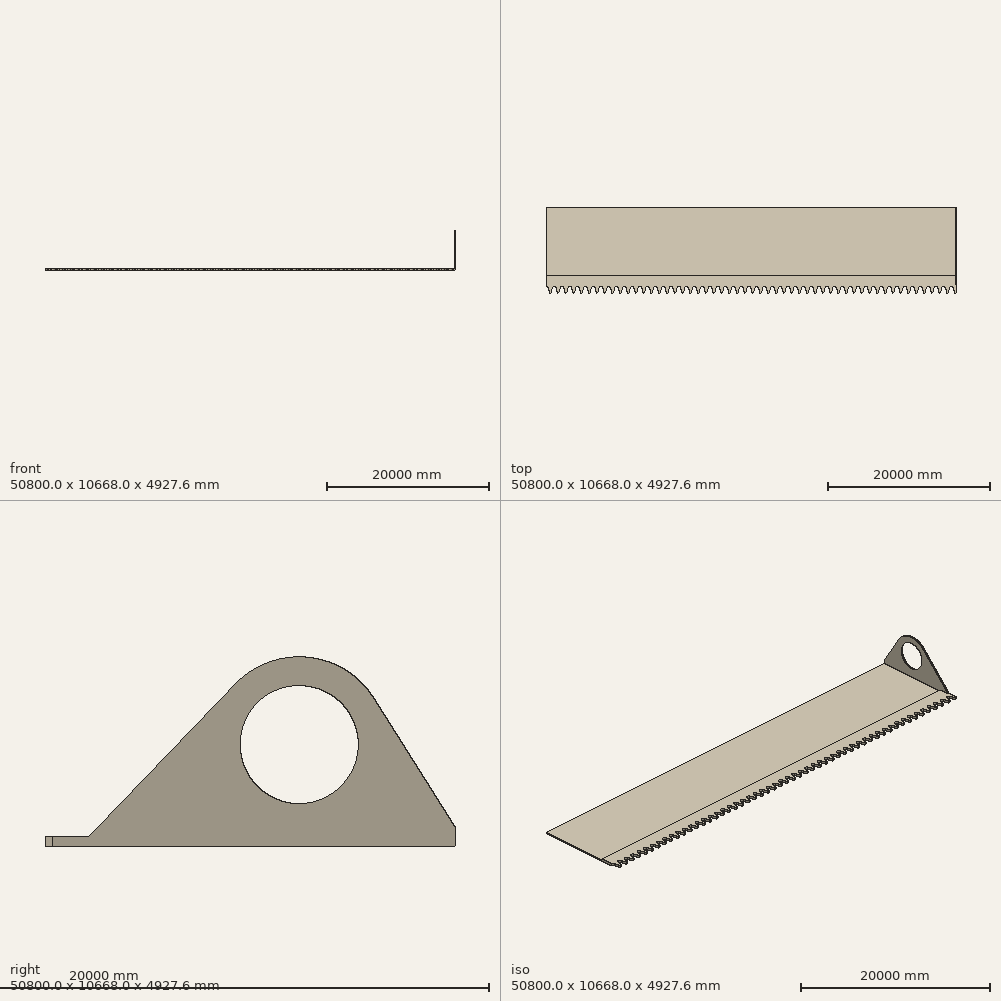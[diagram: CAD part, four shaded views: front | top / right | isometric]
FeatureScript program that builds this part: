
annotation { "Feature Type Name" : "Feature", "Feature Type Description" : "" }
export const myFeature = defineFeature(function(context is Context, id is Id, definition is map)
    precondition{}
    {
        {
            var Q0;
            Q0=qCreatedBy(makeId("Top.planeOp"),FACE);
            var sketch = newSketch(context, id + "F0", { "sketchPlane" : qUnion([Q0])});
            skLineSegment(sketch, "E0", {"start": v(-25432.17, 2645.31) * mm, "end": v(25367.83, 2645.31) * mm});
            skLineSegment(sketch, "E1", {"start": v(25367.83, 2645.31) * mm, "end": v(25367.83, -5736.69) * mm});
            skLineSegment(sketch, "E2", {"start": v(25367.83, -5736.69) * mm, "end": v(-25432.17, -5736.69) * mm});
            skLineSegment(sketch, "E3", {"start": v(-25432.17, -5736.69) * mm, "end": v(-25432.17, 2645.31) * mm});
            skSolve(sketch);
        }
        {
            var Q0;
            Q0 = qSketchRegion(id + "F0", true);
            extrude(context, id + "F1", {"entities" : qUnion([Q0]), "depth" : 101.6 * mm, "offsetDistance" : 25.4 * mm});
        }
        {
            var Q0;
            Q0=makeQuery(id+"F1.opExtrude","SWEPT_FACE",FACE,{"disambiguationData":[OSD([sQuery(id+"F0.wireOp",EDGE,"E2")])]});
            var sketch = newSketch(context, id + "F2", { "sketchPlane" : qUnion([Q0])});
            skLineSegment(sketch, "E4", {"start": v(-25432.17, 0) * mm, "end": v(-25432.17, 254) * mm});
            skLineSegment(sketch, "E5", {"start": v(-25432.17, 254) * mm, "end": v(25367.83, 254) * mm});
            skLineSegment(sketch, "E6", {"start": v(25367.83, 254) * mm, "end": v(25367.83, 0) * mm});
            skLineSegment(sketch, "E7", {"start": v(25367.83, 0) * mm, "end": v(-25432.17, 0) * mm});
            skSolve(sketch);
        }
        {
            var Q0;
            Q0 = qSketchRegion(id + "F2", true);
            extrude(context, id + "F3", {"entities" : qUnion([Q0]), "operationType" : NewBodyOperationType.ADD, "depth" : 2286 * mm, "offsetDistance" : 25.4 * mm});
        }
        {
            var Q0;
            Q0=makeQuery(id+"F3.opExtrude","SWEPT_FACE",FACE,{"disambiguationData":[OSD([sQuery(id+"F2.wireOp",EDGE,"E5")])]});
            var sketch = newSketch(context, id + "F4", { "sketchPlane" : qUnion([Q0])});
            skArc(sketch, "E8", {"start": v(-25211.32, -7328.64) * mm, "mid": v(-25292.95, -7206.36) * mm, "end": v(-25432.17, -7159.09) * mm});
            skArc(sketch, "E9", {"start": v(-24466.97, -7159.09) * mm, "mid": v(-24606.18, -7206.36) * mm, "end": v(-24687.8, -7328.64) * mm});
            skLineSegment(sketch, "E10", {"start": v(-24949.57, -8022.69) * mm, "end": v(-24873.37, -8022.69) * mm});
            skLineSegment(sketch, "E11", {"start": v(-24949.57, -8022.69) * mm, "end": v(-25025.77, -8022.69) * mm});
            skLineSegment(sketch, "E12", {"start": v(-25025.77, -8022.69) * mm, "end": v(-25211.32, -7328.64) * mm});
            skLineSegment(sketch, "E13", {"start": v(-24873.37, -8022.69) * mm, "end": v(-24687.8, -7328.64) * mm});
            skArc(sketch, "E14.1.0.0", {"start": v(-24246.12, -7328.64) * mm, "mid": v(-24327.75, -7206.36) * mm, "end": v(-24466.97, -7159.09) * mm});
            skLineSegment(sketch, "E14.1.0.1", {"start": v(-24060.57, -8022.69) * mm, "end": v(-24246.12, -7328.64) * mm});
            skLineSegment(sketch, "E14.1.0.2", {"start": v(-23984.37, -8022.69) * mm, "end": v(-24060.57, -8022.69) * mm});
            skLineSegment(sketch, "E14.1.0.3", {"start": v(-23984.37, -8022.69) * mm, "end": v(-23908.17, -8022.69) * mm});
            skLineSegment(sketch, "E14.1.0.4", {"start": v(-23908.17, -8022.69) * mm, "end": v(-23722.6, -7328.64) * mm});
            skArc(sketch, "E14.1.0.5", {"start": v(-23501.77, -7159.09) * mm, "mid": v(-23640.98, -7206.36) * mm, "end": v(-23722.6, -7328.64) * mm});
            skArc(sketch, "E14.2.0.0", {"start": v(-23280.92, -7328.64) * mm, "mid": v(-23362.55, -7206.36) * mm, "end": v(-23501.77, -7159.09) * mm});
            skLineSegment(sketch, "E14.2.0.1", {"start": v(-23095.37, -8022.69) * mm, "end": v(-23280.92, -7328.64) * mm});
            skLineSegment(sketch, "E14.2.0.2", {"start": v(-23019.17, -8022.69) * mm, "end": v(-23095.37, -8022.69) * mm});
            skLineSegment(sketch, "E14.2.0.3", {"start": v(-23019.17, -8022.69) * mm, "end": v(-22942.97, -8022.69) * mm});
            skLineSegment(sketch, "E14.2.0.4", {"start": v(-22942.97, -8022.69) * mm, "end": v(-22757.4, -7328.64) * mm});
            skArc(sketch, "E14.2.0.5", {"start": v(-22536.57, -7159.09) * mm, "mid": v(-22675.78, -7206.36) * mm, "end": v(-22757.4, -7328.64) * mm});
            skLineSegment(sketch, "E14.direction1", {"start": v(-25432.17, -7387.69) * mm, "end": v(-24466.97, -7387.69) * mm, "construction": true});
            skArc(sketch, "E15.0.3.0", {"start": v(-22315.72, -7328.64) * mm, "mid": v(-22397.35, -7206.36) * mm, "end": v(-22536.57, -7159.09) * mm});
            skLineSegment(sketch, "E15.4.3.0", {"start": v(-22130.17, -8022.69) * mm, "end": v(-22315.72, -7328.64) * mm});
            skLineSegment(sketch, "E15.7.3.0", {"start": v(-22053.97, -8022.69) * mm, "end": v(-22130.17, -8022.69) * mm});
            skLineSegment(sketch, "E15.10.3.0", {"start": v(-22053.97, -8022.69) * mm, "end": v(-21977.77, -8022.69) * mm});
            skLineSegment(sketch, "E15.13.3.0", {"start": v(-21977.77, -8022.69) * mm, "end": v(-21792.2, -7328.64) * mm});
            skArc(sketch, "E15.16.3.0", {"start": v(-21571.37, -7159.09) * mm, "mid": v(-21710.58, -7206.36) * mm, "end": v(-21792.2, -7328.64) * mm});
            skArc(sketch, "E15.0.4.0", {"start": v(-21350.52, -7328.64) * mm, "mid": v(-21432.15, -7206.36) * mm, "end": v(-21571.37, -7159.09) * mm});
            skLineSegment(sketch, "E15.4.4.0", {"start": v(-21164.97, -8022.69) * mm, "end": v(-21350.52, -7328.64) * mm});
            skLineSegment(sketch, "E15.7.4.0", {"start": v(-21088.77, -8022.69) * mm, "end": v(-21164.97, -8022.69) * mm});
            skLineSegment(sketch, "E15.10.4.0", {"start": v(-21088.77, -8022.69) * mm, "end": v(-21012.57, -8022.69) * mm});
            skLineSegment(sketch, "E15.13.4.0", {"start": v(-21012.57, -8022.69) * mm, "end": v(-20827, -7328.64) * mm});
            skArc(sketch, "E15.16.4.0", {"start": v(-20606.17, -7159.09) * mm, "mid": v(-20745.38, -7206.36) * mm, "end": v(-20827, -7328.64) * mm});
            skArc(sketch, "E15.0.5.0", {"start": v(-20385.32, -7328.64) * mm, "mid": v(-20466.95, -7206.36) * mm, "end": v(-20606.17, -7159.09) * mm});
            skLineSegment(sketch, "E15.4.5.0", {"start": v(-20199.77, -8022.69) * mm, "end": v(-20385.32, -7328.64) * mm});
            skLineSegment(sketch, "E15.7.5.0", {"start": v(-20123.57, -8022.69) * mm, "end": v(-20199.77, -8022.69) * mm});
            skLineSegment(sketch, "E15.10.5.0", {"start": v(-20123.57, -8022.69) * mm, "end": v(-20047.37, -8022.69) * mm});
            skLineSegment(sketch, "E15.13.5.0", {"start": v(-20047.37, -8022.69) * mm, "end": v(-19861.8, -7328.64) * mm});
            skArc(sketch, "E15.16.5.0", {"start": v(-19640.97, -7159.09) * mm, "mid": v(-19780.18, -7206.36) * mm, "end": v(-19861.8, -7328.64) * mm});
            skArc(sketch, "E15.0.6.0", {"start": v(-19420.12, -7328.64) * mm, "mid": v(-19501.75, -7206.36) * mm, "end": v(-19640.97, -7159.09) * mm});
            skLineSegment(sketch, "E15.4.6.0", {"start": v(-19234.57, -8022.69) * mm, "end": v(-19420.12, -7328.64) * mm});
            skLineSegment(sketch, "E15.7.6.0", {"start": v(-19158.37, -8022.69) * mm, "end": v(-19234.57, -8022.69) * mm});
            skLineSegment(sketch, "E15.10.6.0", {"start": v(-19158.37, -8022.69) * mm, "end": v(-19082.17, -8022.69) * mm});
            skLineSegment(sketch, "E15.13.6.0", {"start": v(-19082.17, -8022.69) * mm, "end": v(-18896.6, -7328.64) * mm});
            skArc(sketch, "E15.16.6.0", {"start": v(-18675.77, -7159.09) * mm, "mid": v(-18814.98, -7206.36) * mm, "end": v(-18896.6, -7328.64) * mm});
            skArc(sketch, "E15.0.7.0", {"start": v(-18454.92, -7328.64) * mm, "mid": v(-18536.55, -7206.36) * mm, "end": v(-18675.77, -7159.09) * mm});
            skLineSegment(sketch, "E15.4.7.0", {"start": v(-18269.37, -8022.69) * mm, "end": v(-18454.92, -7328.64) * mm});
            skLineSegment(sketch, "E15.7.7.0", {"start": v(-18193.17, -8022.69) * mm, "end": v(-18269.37, -8022.69) * mm});
            skLineSegment(sketch, "E15.10.7.0", {"start": v(-18193.17, -8022.69) * mm, "end": v(-18116.97, -8022.69) * mm});
            skLineSegment(sketch, "E15.13.7.0", {"start": v(-18116.97, -8022.69) * mm, "end": v(-17931.4, -7328.64) * mm});
            skArc(sketch, "E15.16.7.0", {"start": v(-17710.57, -7159.09) * mm, "mid": v(-17849.78, -7206.36) * mm, "end": v(-17931.4, -7328.64) * mm});
            skArc(sketch, "E15.0.8.0", {"start": v(-17489.72, -7328.64) * mm, "mid": v(-17571.35, -7206.36) * mm, "end": v(-17710.57, -7159.09) * mm});
            skLineSegment(sketch, "E15.4.8.0", {"start": v(-17304.17, -8022.69) * mm, "end": v(-17489.72, -7328.64) * mm});
            skLineSegment(sketch, "E15.7.8.0", {"start": v(-17227.97, -8022.69) * mm, "end": v(-17304.17, -8022.69) * mm});
            skLineSegment(sketch, "E15.10.8.0", {"start": v(-17227.97, -8022.69) * mm, "end": v(-17151.77, -8022.69) * mm});
            skLineSegment(sketch, "E15.13.8.0", {"start": v(-17151.77, -8022.69) * mm, "end": v(-16966.2, -7328.64) * mm});
            skArc(sketch, "E15.16.8.0", {"start": v(-16745.37, -7159.09) * mm, "mid": v(-16884.58, -7206.36) * mm, "end": v(-16966.2, -7328.64) * mm});
            skArc(sketch, "E15.0.9.0", {"start": v(-16524.52, -7328.64) * mm, "mid": v(-16606.15, -7206.36) * mm, "end": v(-16745.37, -7159.09) * mm});
            skLineSegment(sketch, "E15.4.9.0", {"start": v(-16338.97, -8022.69) * mm, "end": v(-16524.52, -7328.64) * mm});
            skLineSegment(sketch, "E15.7.9.0", {"start": v(-16262.77, -8022.69) * mm, "end": v(-16338.97, -8022.69) * mm});
            skLineSegment(sketch, "E15.10.9.0", {"start": v(-16262.77, -8022.69) * mm, "end": v(-16186.57, -8022.69) * mm});
            skLineSegment(sketch, "E15.13.9.0", {"start": v(-16186.57, -8022.69) * mm, "end": v(-16001, -7328.64) * mm});
            skArc(sketch, "E15.16.9.0", {"start": v(-15780.17, -7159.09) * mm, "mid": v(-15919.38, -7206.36) * mm, "end": v(-16001, -7328.64) * mm});
            skArc(sketch, "E15.0.10.0", {"start": v(-15559.32, -7328.64) * mm, "mid": v(-15640.95, -7206.36) * mm, "end": v(-15780.17, -7159.09) * mm});
            skLineSegment(sketch, "E15.4.10.0", {"start": v(-15373.77, -8022.69) * mm, "end": v(-15559.32, -7328.64) * mm});
            skLineSegment(sketch, "E15.7.10.0", {"start": v(-15297.57, -8022.69) * mm, "end": v(-15373.77, -8022.69) * mm});
            skLineSegment(sketch, "E15.10.10.0", {"start": v(-15297.57, -8022.69) * mm, "end": v(-15221.37, -8022.69) * mm});
            skLineSegment(sketch, "E15.13.10.0", {"start": v(-15221.37, -8022.69) * mm, "end": v(-15035.8, -7328.64) * mm});
            skArc(sketch, "E15.16.10.0", {"start": v(-14814.97, -7159.09) * mm, "mid": v(-14954.18, -7206.36) * mm, "end": v(-15035.8, -7328.64) * mm});
            skArc(sketch, "E15.0.11.0", {"start": v(-14594.12, -7328.64) * mm, "mid": v(-14675.75, -7206.36) * mm, "end": v(-14814.97, -7159.09) * mm});
            skLineSegment(sketch, "E15.4.11.0", {"start": v(-14408.57, -8022.69) * mm, "end": v(-14594.12, -7328.64) * mm});
            skLineSegment(sketch, "E15.7.11.0", {"start": v(-14332.37, -8022.69) * mm, "end": v(-14408.57, -8022.69) * mm});
            skLineSegment(sketch, "E15.10.11.0", {"start": v(-14332.37, -8022.69) * mm, "end": v(-14256.17, -8022.69) * mm});
            skLineSegment(sketch, "E15.13.11.0", {"start": v(-14256.17, -8022.69) * mm, "end": v(-14070.6, -7328.64) * mm});
            skArc(sketch, "E15.16.11.0", {"start": v(-13849.77, -7159.09) * mm, "mid": v(-13988.98, -7206.36) * mm, "end": v(-14070.6, -7328.64) * mm});
            skArc(sketch, "E15.0.12.0", {"start": v(-13628.92, -7328.64) * mm, "mid": v(-13710.55, -7206.36) * mm, "end": v(-13849.77, -7159.09) * mm});
            skLineSegment(sketch, "E15.4.12.0", {"start": v(-13443.37, -8022.69) * mm, "end": v(-13628.92, -7328.64) * mm});
            skLineSegment(sketch, "E15.7.12.0", {"start": v(-13367.17, -8022.69) * mm, "end": v(-13443.37, -8022.69) * mm});
            skLineSegment(sketch, "E15.10.12.0", {"start": v(-13367.17, -8022.69) * mm, "end": v(-13290.97, -8022.69) * mm});
            skLineSegment(sketch, "E15.13.12.0", {"start": v(-13290.97, -8022.69) * mm, "end": v(-13105.4, -7328.64) * mm});
            skArc(sketch, "E15.16.12.0", {"start": v(-12884.57, -7159.09) * mm, "mid": v(-13023.78, -7206.36) * mm, "end": v(-13105.4, -7328.64) * mm});
            skArc(sketch, "E15.0.13.0", {"start": v(-12663.72, -7328.64) * mm, "mid": v(-12745.35, -7206.36) * mm, "end": v(-12884.57, -7159.09) * mm});
            skLineSegment(sketch, "E15.4.13.0", {"start": v(-12478.17, -8022.69) * mm, "end": v(-12663.72, -7328.64) * mm});
            skLineSegment(sketch, "E15.7.13.0", {"start": v(-12401.97, -8022.69) * mm, "end": v(-12478.17, -8022.69) * mm});
            skLineSegment(sketch, "E15.10.13.0", {"start": v(-12401.97, -8022.69) * mm, "end": v(-12325.77, -8022.69) * mm});
            skLineSegment(sketch, "E15.13.13.0", {"start": v(-12325.77, -8022.69) * mm, "end": v(-12140.2, -7328.64) * mm});
            skArc(sketch, "E15.16.13.0", {"start": v(-11919.37, -7159.09) * mm, "mid": v(-12058.58, -7206.36) * mm, "end": v(-12140.2, -7328.64) * mm});
            skArc(sketch, "E15.0.14.0", {"start": v(-11698.52, -7328.64) * mm, "mid": v(-11780.15, -7206.36) * mm, "end": v(-11919.37, -7159.09) * mm});
            skLineSegment(sketch, "E15.4.14.0", {"start": v(-11512.97, -8022.69) * mm, "end": v(-11698.52, -7328.64) * mm});
            skLineSegment(sketch, "E15.7.14.0", {"start": v(-11436.77, -8022.69) * mm, "end": v(-11512.97, -8022.69) * mm});
            skLineSegment(sketch, "E15.10.14.0", {"start": v(-11436.77, -8022.69) * mm, "end": v(-11360.57, -8022.69) * mm});
            skLineSegment(sketch, "E15.13.14.0", {"start": v(-11360.57, -8022.69) * mm, "end": v(-11175, -7328.64) * mm});
            skArc(sketch, "E15.16.14.0", {"start": v(-10954.17, -7159.09) * mm, "mid": v(-11093.38, -7206.36) * mm, "end": v(-11175, -7328.64) * mm});
            skArc(sketch, "E15.0.15.0", {"start": v(-10733.32, -7328.64) * mm, "mid": v(-10814.95, -7206.36) * mm, "end": v(-10954.17, -7159.09) * mm});
            skLineSegment(sketch, "E15.4.15.0", {"start": v(-10547.77, -8022.69) * mm, "end": v(-10733.32, -7328.64) * mm});
            skLineSegment(sketch, "E15.7.15.0", {"start": v(-10471.57, -8022.69) * mm, "end": v(-10547.77, -8022.69) * mm});
            skLineSegment(sketch, "E15.10.15.0", {"start": v(-10471.57, -8022.69) * mm, "end": v(-10395.37, -8022.69) * mm});
            skLineSegment(sketch, "E15.13.15.0", {"start": v(-10395.37, -8022.69) * mm, "end": v(-10209.8, -7328.64) * mm});
            skArc(sketch, "E15.16.15.0", {"start": v(-9988.97, -7159.09) * mm, "mid": v(-10128.18, -7206.36) * mm, "end": v(-10209.8, -7328.64) * mm});
            skArc(sketch, "E15.0.16.0", {"start": v(-9768.12, -7328.64) * mm, "mid": v(-9849.75, -7206.36) * mm, "end": v(-9988.97, -7159.09) * mm});
            skLineSegment(sketch, "E15.4.16.0", {"start": v(-9582.57, -8022.69) * mm, "end": v(-9768.12, -7328.64) * mm});
            skLineSegment(sketch, "E15.7.16.0", {"start": v(-9506.37, -8022.69) * mm, "end": v(-9582.57, -8022.69) * mm});
            skLineSegment(sketch, "E15.10.16.0", {"start": v(-9506.37, -8022.69) * mm, "end": v(-9430.17, -8022.69) * mm});
            skLineSegment(sketch, "E15.13.16.0", {"start": v(-9430.17, -8022.69) * mm, "end": v(-9244.6, -7328.64) * mm});
            skArc(sketch, "E15.16.16.0", {"start": v(-9023.77, -7159.09) * mm, "mid": v(-9162.98, -7206.36) * mm, "end": v(-9244.6, -7328.64) * mm});
            skArc(sketch, "E15.0.17.0", {"start": v(-8802.92, -7328.64) * mm, "mid": v(-8884.55, -7206.36) * mm, "end": v(-9023.77, -7159.09) * mm});
            skLineSegment(sketch, "E15.4.17.0", {"start": v(-8617.37, -8022.69) * mm, "end": v(-8802.92, -7328.64) * mm});
            skLineSegment(sketch, "E15.7.17.0", {"start": v(-8541.17, -8022.69) * mm, "end": v(-8617.37, -8022.69) * mm});
            skLineSegment(sketch, "E15.10.17.0", {"start": v(-8541.17, -8022.69) * mm, "end": v(-8464.97, -8022.69) * mm});
            skLineSegment(sketch, "E15.13.17.0", {"start": v(-8464.97, -8022.69) * mm, "end": v(-8279.4, -7328.64) * mm});
            skArc(sketch, "E15.16.17.0", {"start": v(-8058.57, -7159.09) * mm, "mid": v(-8197.78, -7206.36) * mm, "end": v(-8279.4, -7328.64) * mm});
            skArc(sketch, "E15.0.18.0", {"start": v(-7837.72, -7328.64) * mm, "mid": v(-7919.35, -7206.36) * mm, "end": v(-8058.57, -7159.09) * mm});
            skLineSegment(sketch, "E15.4.18.0", {"start": v(-7652.17, -8022.69) * mm, "end": v(-7837.72, -7328.64) * mm});
            skLineSegment(sketch, "E15.7.18.0", {"start": v(-7575.97, -8022.69) * mm, "end": v(-7652.17, -8022.69) * mm});
            skLineSegment(sketch, "E15.10.18.0", {"start": v(-7575.97, -8022.69) * mm, "end": v(-7499.77, -8022.69) * mm});
            skLineSegment(sketch, "E15.13.18.0", {"start": v(-7499.77, -8022.69) * mm, "end": v(-7314.2, -7328.64) * mm});
            skArc(sketch, "E15.16.18.0", {"start": v(-7093.37, -7159.09) * mm, "mid": v(-7232.58, -7206.36) * mm, "end": v(-7314.2, -7328.64) * mm});
            skArc(sketch, "E15.0.19.0", {"start": v(-6872.52, -7328.64) * mm, "mid": v(-6954.15, -7206.36) * mm, "end": v(-7093.37, -7159.09) * mm});
            skLineSegment(sketch, "E15.4.19.0", {"start": v(-6686.97, -8022.69) * mm, "end": v(-6872.52, -7328.64) * mm});
            skLineSegment(sketch, "E15.7.19.0", {"start": v(-6610.77, -8022.69) * mm, "end": v(-6686.97, -8022.69) * mm});
            skLineSegment(sketch, "E15.10.19.0", {"start": v(-6610.77, -8022.69) * mm, "end": v(-6534.57, -8022.69) * mm});
            skLineSegment(sketch, "E15.13.19.0", {"start": v(-6534.57, -8022.69) * mm, "end": v(-6349, -7328.64) * mm});
            skArc(sketch, "E15.16.19.0", {"start": v(-6128.17, -7159.09) * mm, "mid": v(-6267.38, -7206.36) * mm, "end": v(-6349, -7328.64) * mm});
            skArc(sketch, "E15.0.20.0", {"start": v(-5907.32, -7328.64) * mm, "mid": v(-5988.95, -7206.36) * mm, "end": v(-6128.17, -7159.09) * mm});
            skLineSegment(sketch, "E15.4.20.0", {"start": v(-5721.77, -8022.69) * mm, "end": v(-5907.32, -7328.64) * mm});
            skLineSegment(sketch, "E15.7.20.0", {"start": v(-5645.57, -8022.69) * mm, "end": v(-5721.77, -8022.69) * mm});
            skLineSegment(sketch, "E15.10.20.0", {"start": v(-5645.57, -8022.69) * mm, "end": v(-5569.37, -8022.69) * mm});
            skLineSegment(sketch, "E15.13.20.0", {"start": v(-5569.37, -8022.69) * mm, "end": v(-5383.8, -7328.64) * mm});
            skArc(sketch, "E15.16.20.0", {"start": v(-5162.97, -7159.09) * mm, "mid": v(-5302.18, -7206.36) * mm, "end": v(-5383.8, -7328.64) * mm});
            skArc(sketch, "E15.0.21.0", {"start": v(-4942.12, -7328.64) * mm, "mid": v(-5023.75, -7206.36) * mm, "end": v(-5162.97, -7159.09) * mm});
            skLineSegment(sketch, "E15.4.21.0", {"start": v(-4756.57, -8022.69) * mm, "end": v(-4942.12, -7328.64) * mm});
            skLineSegment(sketch, "E15.7.21.0", {"start": v(-4680.37, -8022.69) * mm, "end": v(-4756.57, -8022.69) * mm});
            skLineSegment(sketch, "E15.10.21.0", {"start": v(-4680.37, -8022.69) * mm, "end": v(-4604.17, -8022.69) * mm});
            skLineSegment(sketch, "E15.13.21.0", {"start": v(-4604.17, -8022.69) * mm, "end": v(-4418.6, -7328.64) * mm});
            skArc(sketch, "E15.16.21.0", {"start": v(-4197.77, -7159.09) * mm, "mid": v(-4336.98, -7206.36) * mm, "end": v(-4418.6, -7328.64) * mm});
            skArc(sketch, "E15.0.22.0", {"start": v(-3976.92, -7328.64) * mm, "mid": v(-4058.55, -7206.36) * mm, "end": v(-4197.77, -7159.09) * mm});
            skLineSegment(sketch, "E15.4.22.0", {"start": v(-3791.37, -8022.69) * mm, "end": v(-3976.92, -7328.64) * mm});
            skLineSegment(sketch, "E15.7.22.0", {"start": v(-3715.17, -8022.69) * mm, "end": v(-3791.37, -8022.69) * mm});
            skLineSegment(sketch, "E15.10.22.0", {"start": v(-3715.17, -8022.69) * mm, "end": v(-3638.97, -8022.69) * mm});
            skLineSegment(sketch, "E15.13.22.0", {"start": v(-3638.97, -8022.69) * mm, "end": v(-3453.4, -7328.64) * mm});
            skArc(sketch, "E15.16.22.0", {"start": v(-3232.57, -7159.09) * mm, "mid": v(-3371.78, -7206.36) * mm, "end": v(-3453.4, -7328.64) * mm});
            skArc(sketch, "E15.0.23.0", {"start": v(-3011.72, -7328.64) * mm, "mid": v(-3093.35, -7206.36) * mm, "end": v(-3232.57, -7159.09) * mm});
            skLineSegment(sketch, "E15.4.23.0", {"start": v(-2826.17, -8022.69) * mm, "end": v(-3011.72, -7328.64) * mm});
            skLineSegment(sketch, "E15.7.23.0", {"start": v(-2749.97, -8022.69) * mm, "end": v(-2826.17, -8022.69) * mm});
            skLineSegment(sketch, "E15.10.23.0", {"start": v(-2749.97, -8022.69) * mm, "end": v(-2673.77, -8022.69) * mm});
            skLineSegment(sketch, "E15.13.23.0", {"start": v(-2673.77, -8022.69) * mm, "end": v(-2488.2, -7328.64) * mm});
            skArc(sketch, "E15.16.23.0", {"start": v(-2267.37, -7159.09) * mm, "mid": v(-2406.58, -7206.36) * mm, "end": v(-2488.2, -7328.64) * mm});
            skArc(sketch, "E15.0.24.0", {"start": v(-2046.52, -7328.64) * mm, "mid": v(-2128.15, -7206.36) * mm, "end": v(-2267.37, -7159.09) * mm});
            skLineSegment(sketch, "E15.4.24.0", {"start": v(-1860.97, -8022.69) * mm, "end": v(-2046.52, -7328.64) * mm});
            skLineSegment(sketch, "E15.7.24.0", {"start": v(-1784.77, -8022.69) * mm, "end": v(-1860.97, -8022.69) * mm});
            skLineSegment(sketch, "E15.10.24.0", {"start": v(-1784.77, -8022.69) * mm, "end": v(-1708.57, -8022.69) * mm});
            skLineSegment(sketch, "E15.13.24.0", {"start": v(-1708.57, -8022.69) * mm, "end": v(-1523, -7328.64) * mm});
            skArc(sketch, "E15.16.24.0", {"start": v(-1302.17, -7159.09) * mm, "mid": v(-1441.38, -7206.36) * mm, "end": v(-1523, -7328.64) * mm});
            skArc(sketch, "E15.0.25.0", {"start": v(-1081.32, -7328.64) * mm, "mid": v(-1162.95, -7206.36) * mm, "end": v(-1302.17, -7159.09) * mm});
            skLineSegment(sketch, "E15.4.25.0", {"start": v(-895.77, -8022.69) * mm, "end": v(-1081.32, -7328.64) * mm});
            skLineSegment(sketch, "E15.7.25.0", {"start": v(-819.57, -8022.69) * mm, "end": v(-895.77, -8022.69) * mm});
            skLineSegment(sketch, "E15.10.25.0", {"start": v(-819.57, -8022.69) * mm, "end": v(-743.37, -8022.69) * mm});
            skLineSegment(sketch, "E15.13.25.0", {"start": v(-743.37, -8022.69) * mm, "end": v(-557.8, -7328.64) * mm});
            skArc(sketch, "E15.16.25.0", {"start": v(-336.97, -7159.09) * mm, "mid": v(-476.18, -7206.36) * mm, "end": v(-557.8, -7328.64) * mm});
            skArc(sketch, "E15.0.26.0", {"start": v(-116.12, -7328.64) * mm, "mid": v(-197.75, -7206.36) * mm, "end": v(-336.97, -7159.09) * mm});
            skLineSegment(sketch, "E15.4.26.0", {"start": v(69.43, -8022.69) * mm, "end": v(-116.12, -7328.64) * mm});
            skLineSegment(sketch, "E15.7.26.0", {"start": v(145.63, -8022.69) * mm, "end": v(69.43, -8022.69) * mm});
            skLineSegment(sketch, "E15.10.26.0", {"start": v(145.63, -8022.69) * mm, "end": v(221.83, -8022.69) * mm});
            skLineSegment(sketch, "E15.13.26.0", {"start": v(221.83, -8022.69) * mm, "end": v(407.4, -7328.64) * mm});
            skArc(sketch, "E15.16.26.0", {"start": v(628.23, -7159.09) * mm, "mid": v(489.02, -7206.36) * mm, "end": v(407.4, -7328.64) * mm});
            skArc(sketch, "E15.0.27.0", {"start": v(849.08, -7328.64) * mm, "mid": v(767.45, -7206.36) * mm, "end": v(628.23, -7159.09) * mm});
            skLineSegment(sketch, "E15.4.27.0", {"start": v(1034.63, -8022.69) * mm, "end": v(849.08, -7328.64) * mm});
            skLineSegment(sketch, "E15.7.27.0", {"start": v(1110.83, -8022.69) * mm, "end": v(1034.63, -8022.69) * mm});
            skLineSegment(sketch, "E15.10.27.0", {"start": v(1110.83, -8022.69) * mm, "end": v(1187.03, -8022.69) * mm});
            skLineSegment(sketch, "E15.13.27.0", {"start": v(1187.03, -8022.69) * mm, "end": v(1372.6, -7328.64) * mm});
            skArc(sketch, "E15.16.27.0", {"start": v(1593.43, -7159.09) * mm, "mid": v(1454.22, -7206.36) * mm, "end": v(1372.6, -7328.64) * mm});
            skArc(sketch, "E15.0.28.0", {"start": v(1814.28, -7328.64) * mm, "mid": v(1732.65, -7206.36) * mm, "end": v(1593.43, -7159.09) * mm});
            skLineSegment(sketch, "E15.4.28.0", {"start": v(1999.83, -8022.69) * mm, "end": v(1814.28, -7328.64) * mm});
            skLineSegment(sketch, "E15.7.28.0", {"start": v(2076.03, -8022.69) * mm, "end": v(1999.83, -8022.69) * mm});
            skLineSegment(sketch, "E15.10.28.0", {"start": v(2076.03, -8022.69) * mm, "end": v(2152.23, -8022.69) * mm});
            skLineSegment(sketch, "E15.13.28.0", {"start": v(2152.23, -8022.69) * mm, "end": v(2337.8, -7328.64) * mm});
            skArc(sketch, "E15.16.28.0", {"start": v(2558.63, -7159.09) * mm, "mid": v(2419.42, -7206.36) * mm, "end": v(2337.8, -7328.64) * mm});
            skArc(sketch, "E15.0.29.0", {"start": v(2779.48, -7328.64) * mm, "mid": v(2697.85, -7206.36) * mm, "end": v(2558.63, -7159.09) * mm});
            skLineSegment(sketch, "E15.4.29.0", {"start": v(2965.03, -8022.69) * mm, "end": v(2779.48, -7328.64) * mm});
            skLineSegment(sketch, "E15.7.29.0", {"start": v(3041.23, -8022.69) * mm, "end": v(2965.03, -8022.69) * mm});
            skLineSegment(sketch, "E15.10.29.0", {"start": v(3041.23, -8022.69) * mm, "end": v(3117.43, -8022.69) * mm});
            skLineSegment(sketch, "E15.13.29.0", {"start": v(3117.43, -8022.69) * mm, "end": v(3303, -7328.64) * mm});
            skArc(sketch, "E15.16.29.0", {"start": v(3523.83, -7159.09) * mm, "mid": v(3384.62, -7206.36) * mm, "end": v(3303, -7328.64) * mm});
            skArc(sketch, "E15.0.30.0", {"start": v(3744.68, -7328.64) * mm, "mid": v(3663.05, -7206.36) * mm, "end": v(3523.83, -7159.09) * mm});
            skLineSegment(sketch, "E15.4.30.0", {"start": v(3930.23, -8022.69) * mm, "end": v(3744.68, -7328.64) * mm});
            skLineSegment(sketch, "E15.7.30.0", {"start": v(4006.43, -8022.69) * mm, "end": v(3930.23, -8022.69) * mm});
            skLineSegment(sketch, "E15.10.30.0", {"start": v(4006.43, -8022.69) * mm, "end": v(4082.63, -8022.69) * mm});
            skLineSegment(sketch, "E15.13.30.0", {"start": v(4082.63, -8022.69) * mm, "end": v(4268.2, -7328.64) * mm});
            skArc(sketch, "E15.16.30.0", {"start": v(4489.03, -7159.09) * mm, "mid": v(4349.82, -7206.36) * mm, "end": v(4268.2, -7328.64) * mm});
            skArc(sketch, "E15.0.31.0", {"start": v(4709.88, -7328.64) * mm, "mid": v(4628.25, -7206.36) * mm, "end": v(4489.03, -7159.09) * mm});
            skLineSegment(sketch, "E15.4.31.0", {"start": v(4895.43, -8022.69) * mm, "end": v(4709.88, -7328.64) * mm});
            skLineSegment(sketch, "E15.7.31.0", {"start": v(4971.63, -8022.69) * mm, "end": v(4895.43, -8022.69) * mm});
            skLineSegment(sketch, "E15.10.31.0", {"start": v(4971.63, -8022.69) * mm, "end": v(5047.83, -8022.69) * mm});
            skLineSegment(sketch, "E15.13.31.0", {"start": v(5047.83, -8022.69) * mm, "end": v(5233.4, -7328.64) * mm});
            skArc(sketch, "E15.16.31.0", {"start": v(5454.23, -7159.09) * mm, "mid": v(5315.02, -7206.36) * mm, "end": v(5233.4, -7328.64) * mm});
            skArc(sketch, "E15.0.32.0", {"start": v(5675.08, -7328.64) * mm, "mid": v(5593.45, -7206.36) * mm, "end": v(5454.23, -7159.09) * mm});
            skLineSegment(sketch, "E15.4.32.0", {"start": v(5860.63, -8022.69) * mm, "end": v(5675.08, -7328.64) * mm});
            skLineSegment(sketch, "E15.7.32.0", {"start": v(5936.83, -8022.69) * mm, "end": v(5860.63, -8022.69) * mm});
            skLineSegment(sketch, "E15.10.32.0", {"start": v(5936.83, -8022.69) * mm, "end": v(6013.03, -8022.69) * mm});
            skLineSegment(sketch, "E15.13.32.0", {"start": v(6013.03, -8022.69) * mm, "end": v(6198.6, -7328.64) * mm});
            skArc(sketch, "E15.16.32.0", {"start": v(6419.43, -7159.09) * mm, "mid": v(6280.22, -7206.36) * mm, "end": v(6198.6, -7328.64) * mm});
            skArc(sketch, "E15.0.33.0", {"start": v(6640.28, -7328.64) * mm, "mid": v(6558.65, -7206.36) * mm, "end": v(6419.43, -7159.09) * mm});
            skLineSegment(sketch, "E15.4.33.0", {"start": v(6825.83, -8022.69) * mm, "end": v(6640.28, -7328.64) * mm});
            skLineSegment(sketch, "E15.7.33.0", {"start": v(6902.03, -8022.69) * mm, "end": v(6825.83, -8022.69) * mm});
            skLineSegment(sketch, "E15.10.33.0", {"start": v(6902.03, -8022.69) * mm, "end": v(6978.23, -8022.69) * mm});
            skLineSegment(sketch, "E15.13.33.0", {"start": v(6978.23, -8022.69) * mm, "end": v(7163.8, -7328.64) * mm});
            skArc(sketch, "E15.16.33.0", {"start": v(7384.63, -7159.09) * mm, "mid": v(7245.42, -7206.36) * mm, "end": v(7163.8, -7328.64) * mm});
            skArc(sketch, "E15.0.34.0", {"start": v(7605.48, -7328.64) * mm, "mid": v(7523.85, -7206.36) * mm, "end": v(7384.63, -7159.09) * mm});
            skLineSegment(sketch, "E15.4.34.0", {"start": v(7791.03, -8022.69) * mm, "end": v(7605.48, -7328.64) * mm});
            skLineSegment(sketch, "E15.7.34.0", {"start": v(7867.23, -8022.69) * mm, "end": v(7791.03, -8022.69) * mm});
            skLineSegment(sketch, "E15.10.34.0", {"start": v(7867.23, -8022.69) * mm, "end": v(7943.43, -8022.69) * mm});
            skLineSegment(sketch, "E15.13.34.0", {"start": v(7943.43, -8022.69) * mm, "end": v(8129, -7328.64) * mm});
            skArc(sketch, "E15.16.34.0", {"start": v(8349.83, -7159.09) * mm, "mid": v(8210.62, -7206.36) * mm, "end": v(8129, -7328.64) * mm});
            skArc(sketch, "E15.0.35.0", {"start": v(8570.68, -7328.64) * mm, "mid": v(8489.05, -7206.36) * mm, "end": v(8349.83, -7159.09) * mm});
            skLineSegment(sketch, "E15.4.35.0", {"start": v(8756.23, -8022.69) * mm, "end": v(8570.68, -7328.64) * mm});
            skLineSegment(sketch, "E15.7.35.0", {"start": v(8832.43, -8022.69) * mm, "end": v(8756.23, -8022.69) * mm});
            skLineSegment(sketch, "E15.10.35.0", {"start": v(8832.43, -8022.69) * mm, "end": v(8908.63, -8022.69) * mm});
            skLineSegment(sketch, "E15.13.35.0", {"start": v(8908.63, -8022.69) * mm, "end": v(9094.2, -7328.64) * mm});
            skArc(sketch, "E15.16.35.0", {"start": v(9315.03, -7159.09) * mm, "mid": v(9175.82, -7206.36) * mm, "end": v(9094.2, -7328.64) * mm});
            skArc(sketch, "E15.0.36.0", {"start": v(9535.88, -7328.64) * mm, "mid": v(9454.25, -7206.36) * mm, "end": v(9315.03, -7159.09) * mm});
            skLineSegment(sketch, "E15.4.36.0", {"start": v(9721.43, -8022.69) * mm, "end": v(9535.88, -7328.64) * mm});
            skLineSegment(sketch, "E15.7.36.0", {"start": v(9797.63, -8022.69) * mm, "end": v(9721.43, -8022.69) * mm});
            skLineSegment(sketch, "E15.10.36.0", {"start": v(9797.63, -8022.69) * mm, "end": v(9873.83, -8022.69) * mm});
            skLineSegment(sketch, "E15.13.36.0", {"start": v(9873.83, -8022.69) * mm, "end": v(10059.4, -7328.64) * mm});
            skArc(sketch, "E15.16.36.0", {"start": v(10280.23, -7159.09) * mm, "mid": v(10141.02, -7206.36) * mm, "end": v(10059.4, -7328.64) * mm});
            skArc(sketch, "E15.0.37.0", {"start": v(10501.08, -7328.64) * mm, "mid": v(10419.45, -7206.36) * mm, "end": v(10280.23, -7159.09) * mm});
            skLineSegment(sketch, "E15.4.37.0", {"start": v(10686.63, -8022.69) * mm, "end": v(10501.08, -7328.64) * mm});
            skLineSegment(sketch, "E15.7.37.0", {"start": v(10762.83, -8022.69) * mm, "end": v(10686.63, -8022.69) * mm});
            skLineSegment(sketch, "E15.10.37.0", {"start": v(10762.83, -8022.69) * mm, "end": v(10839.03, -8022.69) * mm});
            skLineSegment(sketch, "E15.13.37.0", {"start": v(10839.03, -8022.69) * mm, "end": v(11024.6, -7328.64) * mm});
            skArc(sketch, "E15.16.37.0", {"start": v(11245.43, -7159.09) * mm, "mid": v(11106.22, -7206.36) * mm, "end": v(11024.6, -7328.64) * mm});
            skArc(sketch, "E15.0.38.0", {"start": v(11466.28, -7328.64) * mm, "mid": v(11384.65, -7206.36) * mm, "end": v(11245.43, -7159.09) * mm});
            skLineSegment(sketch, "E15.4.38.0", {"start": v(11651.83, -8022.69) * mm, "end": v(11466.28, -7328.64) * mm});
            skLineSegment(sketch, "E15.7.38.0", {"start": v(11728.03, -8022.69) * mm, "end": v(11651.83, -8022.69) * mm});
            skLineSegment(sketch, "E15.10.38.0", {"start": v(11728.03, -8022.69) * mm, "end": v(11804.23, -8022.69) * mm});
            skLineSegment(sketch, "E15.13.38.0", {"start": v(11804.23, -8022.69) * mm, "end": v(11989.8, -7328.64) * mm});
            skArc(sketch, "E15.16.38.0", {"start": v(12210.63, -7159.09) * mm, "mid": v(12071.42, -7206.36) * mm, "end": v(11989.8, -7328.64) * mm});
            skArc(sketch, "E15.0.39.0", {"start": v(12431.48, -7328.64) * mm, "mid": v(12349.85, -7206.36) * mm, "end": v(12210.63, -7159.09) * mm});
            skLineSegment(sketch, "E15.4.39.0", {"start": v(12617.03, -8022.69) * mm, "end": v(12431.48, -7328.64) * mm});
            skLineSegment(sketch, "E15.7.39.0", {"start": v(12693.23, -8022.69) * mm, "end": v(12617.03, -8022.69) * mm});
            skLineSegment(sketch, "E15.10.39.0", {"start": v(12693.23, -8022.69) * mm, "end": v(12769.43, -8022.69) * mm});
            skLineSegment(sketch, "E15.13.39.0", {"start": v(12769.43, -8022.69) * mm, "end": v(12955, -7328.64) * mm});
            skArc(sketch, "E15.16.39.0", {"start": v(13175.83, -7159.09) * mm, "mid": v(13036.62, -7206.36) * mm, "end": v(12955, -7328.64) * mm});
            skArc(sketch, "E15.0.40.0", {"start": v(13396.68, -7328.64) * mm, "mid": v(13315.05, -7206.36) * mm, "end": v(13175.83, -7159.09) * mm});
            skLineSegment(sketch, "E15.4.40.0", {"start": v(13582.23, -8022.69) * mm, "end": v(13396.68, -7328.64) * mm});
            skLineSegment(sketch, "E15.7.40.0", {"start": v(13658.43, -8022.69) * mm, "end": v(13582.23, -8022.69) * mm});
            skLineSegment(sketch, "E15.10.40.0", {"start": v(13658.43, -8022.69) * mm, "end": v(13734.63, -8022.69) * mm});
            skLineSegment(sketch, "E15.13.40.0", {"start": v(13734.63, -8022.69) * mm, "end": v(13920.2, -7328.64) * mm});
            skArc(sketch, "E15.16.40.0", {"start": v(14141.03, -7159.09) * mm, "mid": v(14001.82, -7206.36) * mm, "end": v(13920.2, -7328.64) * mm});
            skArc(sketch, "E15.0.41.0", {"start": v(14361.88, -7328.64) * mm, "mid": v(14280.25, -7206.36) * mm, "end": v(14141.03, -7159.09) * mm});
            skLineSegment(sketch, "E15.4.41.0", {"start": v(14547.43, -8022.69) * mm, "end": v(14361.88, -7328.64) * mm});
            skLineSegment(sketch, "E15.7.41.0", {"start": v(14623.63, -8022.69) * mm, "end": v(14547.43, -8022.69) * mm});
            skLineSegment(sketch, "E15.10.41.0", {"start": v(14623.63, -8022.69) * mm, "end": v(14699.83, -8022.69) * mm});
            skLineSegment(sketch, "E15.13.41.0", {"start": v(14699.83, -8022.69) * mm, "end": v(14885.4, -7328.64) * mm});
            skArc(sketch, "E15.16.41.0", {"start": v(15106.23, -7159.09) * mm, "mid": v(14967.02, -7206.36) * mm, "end": v(14885.4, -7328.64) * mm});
            skArc(sketch, "E15.0.42.0", {"start": v(15327.08, -7328.64) * mm, "mid": v(15245.45, -7206.36) * mm, "end": v(15106.23, -7159.09) * mm});
            skLineSegment(sketch, "E15.4.42.0", {"start": v(15512.63, -8022.69) * mm, "end": v(15327.08, -7328.64) * mm});
            skLineSegment(sketch, "E15.7.42.0", {"start": v(15588.83, -8022.69) * mm, "end": v(15512.63, -8022.69) * mm});
            skLineSegment(sketch, "E15.10.42.0", {"start": v(15588.83, -8022.69) * mm, "end": v(15665.03, -8022.69) * mm});
            skLineSegment(sketch, "E15.13.42.0", {"start": v(15665.03, -8022.69) * mm, "end": v(15850.6, -7328.64) * mm});
            skArc(sketch, "E15.16.42.0", {"start": v(16071.43, -7159.09) * mm, "mid": v(15932.22, -7206.36) * mm, "end": v(15850.6, -7328.64) * mm});
            skArc(sketch, "E15.0.43.0", {"start": v(16292.28, -7328.64) * mm, "mid": v(16210.65, -7206.36) * mm, "end": v(16071.43, -7159.09) * mm});
            skLineSegment(sketch, "E15.4.43.0", {"start": v(16477.83, -8022.69) * mm, "end": v(16292.28, -7328.64) * mm});
            skLineSegment(sketch, "E15.7.43.0", {"start": v(16554.03, -8022.69) * mm, "end": v(16477.83, -8022.69) * mm});
            skLineSegment(sketch, "E15.10.43.0", {"start": v(16554.03, -8022.69) * mm, "end": v(16630.23, -8022.69) * mm});
            skLineSegment(sketch, "E15.13.43.0", {"start": v(16630.23, -8022.69) * mm, "end": v(16815.8, -7328.64) * mm});
            skArc(sketch, "E15.16.43.0", {"start": v(17036.63, -7159.09) * mm, "mid": v(16897.42, -7206.36) * mm, "end": v(16815.8, -7328.64) * mm});
            skArc(sketch, "E15.0.44.0", {"start": v(17257.48, -7328.64) * mm, "mid": v(17175.85, -7206.36) * mm, "end": v(17036.63, -7159.09) * mm});
            skLineSegment(sketch, "E15.4.44.0", {"start": v(17443.03, -8022.69) * mm, "end": v(17257.48, -7328.64) * mm});
            skLineSegment(sketch, "E15.7.44.0", {"start": v(17519.23, -8022.69) * mm, "end": v(17443.03, -8022.69) * mm});
            skLineSegment(sketch, "E15.10.44.0", {"start": v(17519.23, -8022.69) * mm, "end": v(17595.43, -8022.69) * mm});
            skLineSegment(sketch, "E15.13.44.0", {"start": v(17595.43, -8022.69) * mm, "end": v(17781, -7328.64) * mm});
            skArc(sketch, "E15.16.44.0", {"start": v(18001.83, -7159.09) * mm, "mid": v(17862.62, -7206.36) * mm, "end": v(17781, -7328.64) * mm});
            skArc(sketch, "E15.0.45.0", {"start": v(18222.68, -7328.64) * mm, "mid": v(18141.05, -7206.36) * mm, "end": v(18001.83, -7159.09) * mm});
            skLineSegment(sketch, "E15.4.45.0", {"start": v(18408.23, -8022.69) * mm, "end": v(18222.68, -7328.64) * mm});
            skLineSegment(sketch, "E15.7.45.0", {"start": v(18484.43, -8022.69) * mm, "end": v(18408.23, -8022.69) * mm});
            skLineSegment(sketch, "E15.10.45.0", {"start": v(18484.43, -8022.69) * mm, "end": v(18560.63, -8022.69) * mm});
            skLineSegment(sketch, "E15.13.45.0", {"start": v(18560.63, -8022.69) * mm, "end": v(18746.2, -7328.64) * mm});
            skArc(sketch, "E15.16.45.0", {"start": v(18967.03, -7159.09) * mm, "mid": v(18827.82, -7206.36) * mm, "end": v(18746.2, -7328.64) * mm});
            skArc(sketch, "E15.0.46.0", {"start": v(19187.88, -7328.64) * mm, "mid": v(19106.25, -7206.36) * mm, "end": v(18967.03, -7159.09) * mm});
            skLineSegment(sketch, "E15.4.46.0", {"start": v(19373.43, -8022.69) * mm, "end": v(19187.88, -7328.64) * mm});
            skLineSegment(sketch, "E15.7.46.0", {"start": v(19449.63, -8022.69) * mm, "end": v(19373.43, -8022.69) * mm});
            skLineSegment(sketch, "E15.10.46.0", {"start": v(19449.63, -8022.69) * mm, "end": v(19525.83, -8022.69) * mm});
            skLineSegment(sketch, "E15.13.46.0", {"start": v(19525.83, -8022.69) * mm, "end": v(19711.4, -7328.64) * mm});
            skArc(sketch, "E15.16.46.0", {"start": v(19932.23, -7159.09) * mm, "mid": v(19793.02, -7206.36) * mm, "end": v(19711.4, -7328.64) * mm});
            skArc(sketch, "E15.0.47.0", {"start": v(20153.08, -7328.64) * mm, "mid": v(20071.45, -7206.36) * mm, "end": v(19932.23, -7159.09) * mm});
            skLineSegment(sketch, "E15.4.47.0", {"start": v(20338.63, -8022.69) * mm, "end": v(20153.08, -7328.64) * mm});
            skLineSegment(sketch, "E15.7.47.0", {"start": v(20414.83, -8022.69) * mm, "end": v(20338.63, -8022.69) * mm});
            skLineSegment(sketch, "E15.10.47.0", {"start": v(20414.83, -8022.69) * mm, "end": v(20491.03, -8022.69) * mm});
            skLineSegment(sketch, "E15.13.47.0", {"start": v(20491.03, -8022.69) * mm, "end": v(20676.6, -7328.64) * mm});
            skArc(sketch, "E15.16.47.0", {"start": v(20897.43, -7159.09) * mm, "mid": v(20758.22, -7206.36) * mm, "end": v(20676.6, -7328.64) * mm});
            skArc(sketch, "E15.0.48.0", {"start": v(21118.28, -7328.64) * mm, "mid": v(21036.65, -7206.36) * mm, "end": v(20897.43, -7159.09) * mm});
            skLineSegment(sketch, "E15.4.48.0", {"start": v(21303.83, -8022.69) * mm, "end": v(21118.28, -7328.64) * mm});
            skLineSegment(sketch, "E15.7.48.0", {"start": v(21380.03, -8022.69) * mm, "end": v(21303.83, -8022.69) * mm});
            skLineSegment(sketch, "E15.10.48.0", {"start": v(21380.03, -8022.69) * mm, "end": v(21456.23, -8022.69) * mm});
            skLineSegment(sketch, "E15.13.48.0", {"start": v(21456.23, -8022.69) * mm, "end": v(21641.8, -7328.64) * mm});
            skArc(sketch, "E15.16.48.0", {"start": v(21862.63, -7159.09) * mm, "mid": v(21723.42, -7206.36) * mm, "end": v(21641.8, -7328.64) * mm});
            skArc(sketch, "E15.0.49.0", {"start": v(22083.48, -7328.64) * mm, "mid": v(22001.85, -7206.36) * mm, "end": v(21862.63, -7159.09) * mm});
            skLineSegment(sketch, "E15.4.49.0", {"start": v(22269.03, -8022.69) * mm, "end": v(22083.48, -7328.64) * mm});
            skLineSegment(sketch, "E15.7.49.0", {"start": v(22345.23, -8022.69) * mm, "end": v(22269.03, -8022.69) * mm});
            skLineSegment(sketch, "E15.10.49.0", {"start": v(22345.23, -8022.69) * mm, "end": v(22421.43, -8022.69) * mm});
            skLineSegment(sketch, "E15.13.49.0", {"start": v(22421.43, -8022.69) * mm, "end": v(22607, -7328.64) * mm});
            skArc(sketch, "E15.16.49.0", {"start": v(22827.83, -7159.09) * mm, "mid": v(22688.62, -7206.36) * mm, "end": v(22607, -7328.64) * mm});
            skArc(sketch, "E15.0.50.0", {"start": v(23048.68, -7328.64) * mm, "mid": v(22967.05, -7206.36) * mm, "end": v(22827.83, -7159.09) * mm});
            skLineSegment(sketch, "E15.4.50.0", {"start": v(23234.23, -8022.69) * mm, "end": v(23048.68, -7328.64) * mm});
            skLineSegment(sketch, "E15.7.50.0", {"start": v(23310.43, -8022.69) * mm, "end": v(23234.23, -8022.69) * mm});
            skLineSegment(sketch, "E15.10.50.0", {"start": v(23310.43, -8022.69) * mm, "end": v(23386.63, -8022.69) * mm});
            skLineSegment(sketch, "E15.13.50.0", {"start": v(23386.63, -8022.69) * mm, "end": v(23572.2, -7328.64) * mm});
            skArc(sketch, "E15.16.50.0", {"start": v(23793.03, -7159.09) * mm, "mid": v(23653.82, -7206.36) * mm, "end": v(23572.2, -7328.64) * mm});
            skArc(sketch, "E15.0.51.0", {"start": v(24013.88, -7328.64) * mm, "mid": v(23932.25, -7206.36) * mm, "end": v(23793.03, -7159.09) * mm});
            skLineSegment(sketch, "E15.4.51.0", {"start": v(24199.43, -8022.69) * mm, "end": v(24013.88, -7328.64) * mm});
            skLineSegment(sketch, "E15.7.51.0", {"start": v(24275.63, -8022.69) * mm, "end": v(24199.43, -8022.69) * mm});
            skLineSegment(sketch, "E15.10.51.0", {"start": v(24275.63, -8022.69) * mm, "end": v(24351.83, -8022.69) * mm});
            skLineSegment(sketch, "E15.13.51.0", {"start": v(24351.83, -8022.69) * mm, "end": v(24537.4, -7328.64) * mm});
            skArc(sketch, "E15.16.51.0", {"start": v(24758.23, -7159.09) * mm, "mid": v(24619.02, -7206.36) * mm, "end": v(24537.4, -7328.64) * mm});
            skArc(sketch, "E15.0.52.0", {"start": v(24979.08, -7328.64) * mm, "mid": v(24897.45, -7206.36) * mm, "end": v(24758.23, -7159.09) * mm});
            skLineSegment(sketch, "E15.4.52.0", {"start": v(25164.63, -8022.69) * mm, "end": v(24979.08, -7328.64) * mm});
            skLineSegment(sketch, "E15.7.52.0", {"start": v(25240.83, -8022.69) * mm, "end": v(25164.63, -8022.69) * mm});
            skLineSegment(sketch, "E15.10.52.0", {"start": v(25240.83, -8022.69) * mm, "end": v(25317.03, -8022.69) * mm});
            skLineSegment(sketch, "E15.13.52.0", {"start": v(25317.03, -8022.69) * mm, "end": v(25502.6, -7328.64) * mm});
            skArc(sketch, "E15.16.52.0", {"start": v(25723.43, -7159.09) * mm, "mid": v(25584.22, -7206.36) * mm, "end": v(25502.6, -7328.64) * mm});
            skLineSegment(sketch, "E16", {"start": v(25367.83, -7832.68) * mm, "end": v(25367.83, -8162.97) * mm});
            skLineSegment(sketch, "E17", {"start": v(25367.83, -8162.97) * mm, "end": v(-25432.17, -8162.97) * mm});
            skLineSegment(sketch, "E18", {"start": v(-25432.17, -8162.97) * mm, "end": v(-25432.17, -7159.09) * mm});
            skSolve(sketch);
        }
        {
            var Q0;
            Q0 = qSketchRegion(id + "F4", true);
            extrude(context, id + "F5", {"entities" : qUnion([Q0]), "operationType" : NewBodyOperationType.REMOVE, "oppositeDirection" : true, "depth" : 254 * mm, "offsetDistance" : 25.4 * mm});
        }
        {
            var Q0;
            Q0=makeQuery(id+"F3.boolean.opBoolean","MERGE",FACE,{"derivedFrom":[makeQuery(id+"F1.opExtrude","SWEPT_FACE",FACE,{"disambiguationData":[OSD([sQuery(id+"F0.wireOp",EDGE,"E1")])]}),makeQuery(id+"F3.opExtrude","SWEPT_FACE",FACE,{"disambiguationData":[OSD([sQuery(id+"F2.wireOp",EDGE,"E6")])]})]});
            var sketch = newSketch(context, id + "F6", { "sketchPlane" : qUnion([Q0])});
            skLineSegment(sketch, "E19", {"start": v(-5736.69, 254) * mm, "end": v(-6879.69, 254) * mm});
            skLineSegment(sketch, "E20", {"start": v(-5736.69, 254) * mm, "end": v(-5736.69, 101.6) * mm});
            skLineSegment(sketch, "E21", {"start": v(-5736.69, 101.6) * mm, "end": v(2645.31, 101.6) * mm});
            skLineSegment(sketch, "E22", {"start": v(2645.31, 101.6) * mm, "end": v(2645.31, 482.6) * mm});
            skArc(sketch, "E23", {"start": v(514.96, 3860.94) * mm, "mid": v(-1187.75, 4915.9) * mm, "end": v(-3067.77, 4224.73) * mm});
            skLineSegment(sketch, "E24", {"start": v(-6879.69, 254) * mm, "end": v(-3067.77, 4224.73) * mm});
            skLineSegment(sketch, "E25", {"start": v(2645.31, 482.6) * mm, "end": v(514.96, 3860.94) * mm});
            skCircle(sketch, "E26", {"center": v(-1418.69, 2641.6) * mm, "radius": 1536.7 * mm});
            skSolve(sketch);
        }
        {
            var Q0;
            Q0 = qSketchRegion(id + "F6", true);
            extrude(context, id + "F7", {"entities" : qUnion([Q0]), "operationType" : NewBodyOperationType.ADD, "oppositeDirection" : true, "depth" : 152.4 * mm, "offsetDistance" : 25.4 * mm});
        }
    });
